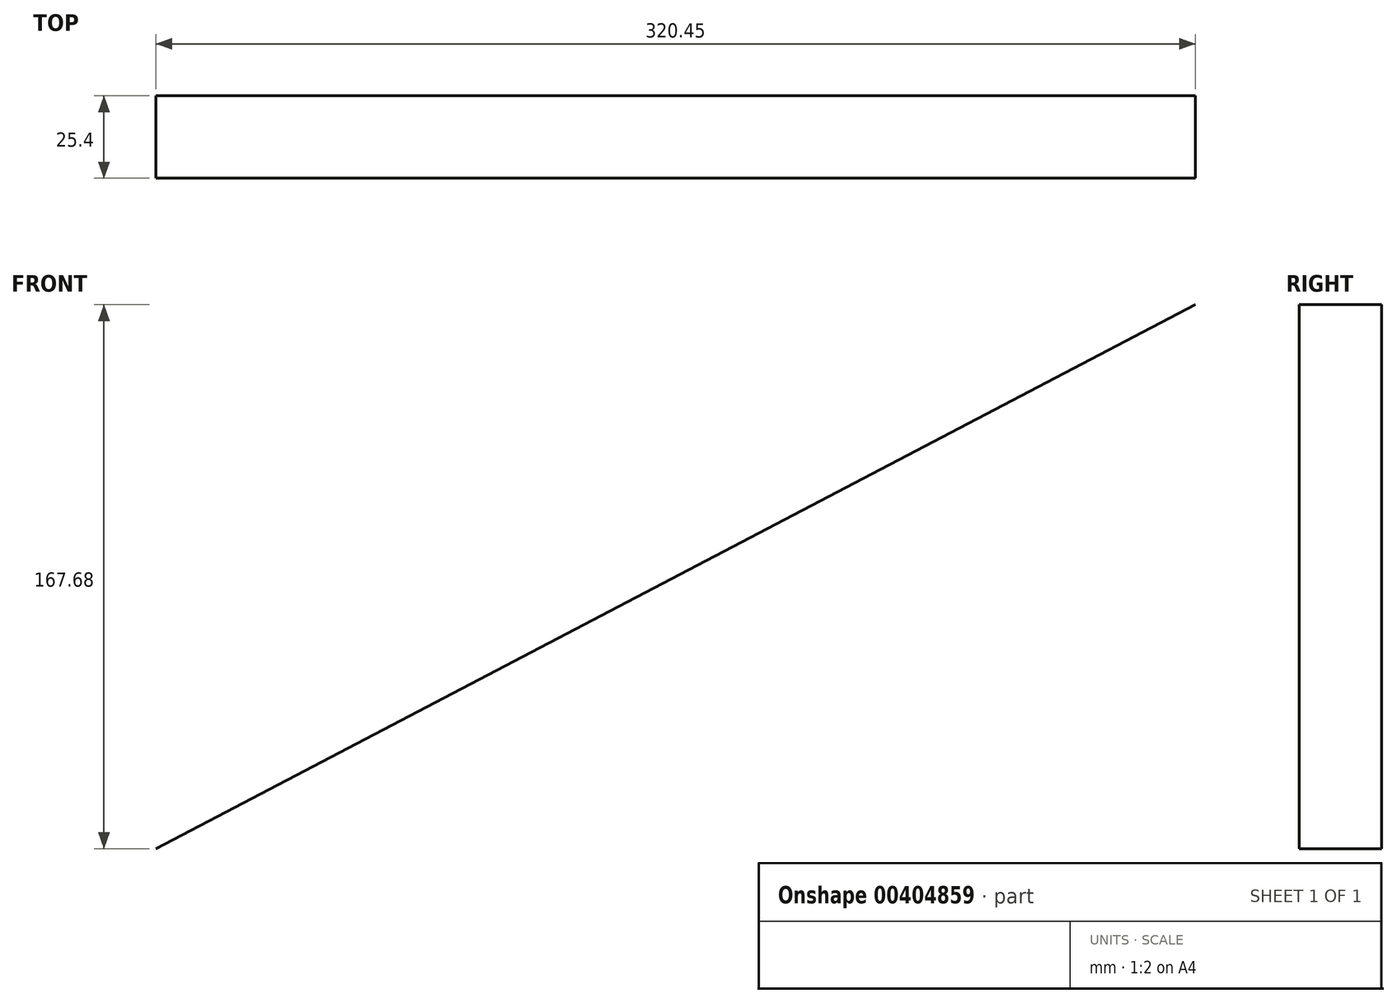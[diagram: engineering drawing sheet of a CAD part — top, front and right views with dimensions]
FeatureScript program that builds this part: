
annotation { "Feature Type Name" : "Feature", "Feature Type Description" : "" }
export const myFeature = defineFeature(function(context is Context, id is Id, definition is map)
    precondition{}
    {
        {
            var Q0;
            Q0=qCreatedBy(makeId("Front.planeOp"),FACE);
            cPlane(context, id + "F0", {"entities" : qUnion([Q0]), "cplaneType" : CPlaneType.OFFSET, "offset" : 25.4 * mm, "width" : 152.4 * mm, "height" : 152.4 * mm});
        }
        {
            var Q0;
            Q0=qCreatedBy(id+"F0.planeOp",FACE);
            var sketch = newSketch(context, id + "F1", { "sketchPlane" : qUnion([Q0])});
            skLineSegment(sketch, "E0", {"start": v(72.44, 67.54) * mm, "end": v(61, 22.65) * mm});
            skLineSegment(sketch, "E1", {"start": v(61, 22.65) * mm, "end": v(246.22, 130.76) * mm});
            skLineSegment(sketch, "E2", {"start": v(246.22, 130.76) * mm, "end": v(64.13, 34.9) * mm});
            skLineSegment(sketch, "E3", {"start": v(72.44, 67.54) * mm, "end": v(392.89, 235.22) * mm});
            skSolve(sketch);
        }
        {
            var Q0;
            Q0=sQuery(id+"F1.wireOp",EDGE,"E3");
            extrude(context, id + "F2", {"bodyType" : ToolBodyType.SURFACE, "surfaceEntities" : qUnion([Q0]), "oppositeDirection" : true, "depth" : 25.4 * mm});
        }
    });
